# Revit family: NBS_HeatraeSadia_StrgWtrHtrsElctrc_CateringSupremeCountertop
name_source: partatom
category: Plumbing Fixtures
revit_build: Autodesk Revit 2014 (Build: 20130709_2115(x64)
units: mm (PartAtom-declared; Revit-internal decimal feet)

## types (1)
- CateringSupremeCountertop
    Accessories = Digital programmer (95:970:124), Securing clamp (95:970:154), Stainless steel drip tray (95:970:152)
    Arrangement = Single point – mains supply
    AssetType = Fixed
    BIMObjectName = NBS_HeatraeSadia_StorageWaterHeatersElectric_CateringSupremeCountertop
    CW Connection = Yes
    CasingFinish = Stainless steel
    Color = Natural
    Control = Tap handle
    Depth = 360 mm  [stored 1.1811 ft]
    Description = Water boiling heater
    DurationUnit = year
    Features = Integral scale inhibitor technology, self-diagnostic service indicator, supplied drip tray, energy efficient
    Fixing = Counter top installation
    FlowRate = To suit draw off requirements
    HW Connection = No
    HeatOutput = 0
    HeatTransferSurfaceArea = 0
    Height = 535 mm  [stored 1.75525 ft]
    IfcExportAs = IfcBoilerType
    IfcExportType = WATER
    IsWaterStorageHeater = Yes
    ManufacturerName = Heatrae Sadia
    ManufacturerURL = www.heatraesadia.com
    Material = Outer casing: Stainless steel; Water container: High quality 304 grade (1.4301) stainless steel
    ModelNumber = 95:200:264
    ModelReference = Catering Supreme Countertop
    NBSCertification = http://www.nationalbimlibrary.com
    NBSDescription = Storage water heaters, electric
    NBSReference = 90-15-35/440
    Name = StorageWaterHeatersElectric_CateringSupremeCountertop_HeatraeSadia
    NominalEfficiency = 0
    NominalEnergyConsumption = 0 mm  [stored 0 ft]
    NominalHeight = 535 mm  [stored 1.75525 ft]
    NominalLength = 240 mm  [stored 0.787402 ft]
    NominalPartLoadRatio = 0 mm  [stored 0 ft]
    NominalWidth = 360 mm  [stored 1.1811 ft]
    OutletTemperatureRange = 100
    PartialLoadEfficiencyCurves = 0
    PressureRating = 0
    ProductInformation = www.heatraesadia.com/docs/Drinking_water_brochure.pdf
    Rating = 3 kW
    SafetyFeatures = Thermal cut-out
    Size = 535 x 240 x 360 mm
    StorageWaterHeaterMaterial = NBS_Concept
    ThermalInsulation = Polystyrene
    ThirdPartyCertification = Kiwa approved
    Uniclass2 = 90-90-46/428
    Uniclass2015Description = Electric storage water heaters
    Uniclass2015Reference = Pr_60_60_96_28
    Uniclass2015Version = Products v1.1
    Vent Connection = Yes
    Version = 1
    WarrantyDurationParts = 2
    WarrantyDurationUnit = year
    WarrantyStartDate = 1900-12-31T23:59:59
    Waste Connection = No
    WaterInletTemperatureRange = 0
    WaterStorageCapacity = 9
    Weight = 29
    Width = 240 mm  [stored 0.787402 ft]

note: [stored X ft] marks values corroborated as IEEE doubles in the binary element streams (Revit-internal decimal feet)

## geometry (parser evidence)
native form markers: Sweep x1
no freeform markers — native parametric forms only
